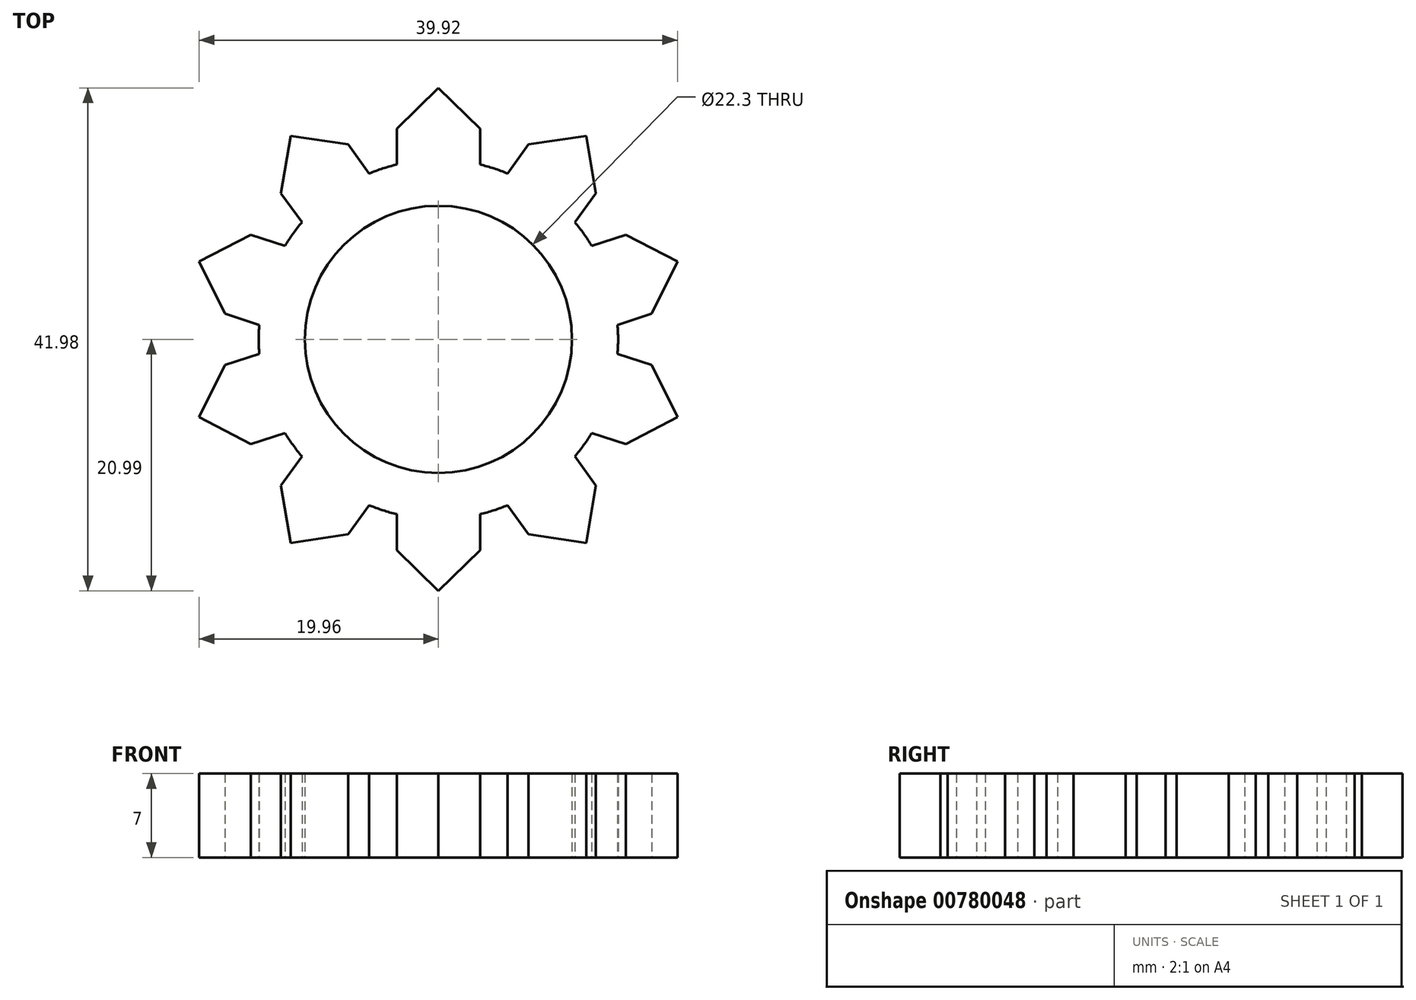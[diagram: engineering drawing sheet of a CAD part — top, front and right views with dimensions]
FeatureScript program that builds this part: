
annotation { "Feature Type Name" : "Feature", "Feature Type Description" : "" }
export const myFeature = defineFeature(function(context is Context, id is Id, definition is map)
    precondition{}
    {
        {
            var Q0;
            Q0=qCreatedBy(makeId("Top.planeOp"),FACE);
            var sketch = newSketch(context, id + "F0", { "sketchPlane" : qUnion([Q0])});
            skCircle(sketch, "E0", {"center": v(0, 0) * mm, "radius": 11.15 * mm});
            skCircle(sketch, "E1", {"center": v(0, 0) * mm, "radius": 15 * mm});
            skLineSegment(sketch, "E2", {"start": v(3.47, 14.6) * mm, "end": v(3.47, 17.6) * mm});
            skLineSegment(sketch, "E3", {"start": v(3.47, 17.6) * mm, "end": v(0, 21) * mm});
            skLineSegment(sketch, "E4.MirrorCS", {"start": v(-3.47, 14.6) * mm, "end": v(-3.47, 17.6) * mm});
            skLineSegment(sketch, "E5.MirrorCS", {"start": v(-3.47, 17.6) * mm, "end": v(0, 21) * mm});
            skLineSegment(sketch, "E6.1.0", {"start": v(-13.15, 12.2) * mm, "end": v(-12.34, 16.98) * mm});
            skLineSegment(sketch, "E6.1.1", {"start": v(-11.39, 9.77) * mm, "end": v(-13.15, 12.2) * mm});
            skLineSegment(sketch, "E6.1.2", {"start": v(-7.53, 16.27) * mm, "end": v(-12.34, 16.98) * mm});
            skLineSegment(sketch, "E6.1.3", {"start": v(-5.77, 13.85) * mm, "end": v(-7.53, 16.27) * mm});
            skLineSegment(sketch, "E6.1.4", {"start": v(-13.15, 12.2) * mm, "end": v(-12.34, 16.98) * mm});
            skLineSegment(sketch, "E6.2.0", {"start": v(-17.8, 2.13) * mm, "end": v(-19.96, 6.49) * mm});
            skLineSegment(sketch, "E6.2.1", {"start": v(-14.95, 1.2) * mm, "end": v(-17.8, 2.13) * mm});
            skLineSegment(sketch, "E6.2.2", {"start": v(-15.66, 8.74) * mm, "end": v(-19.96, 6.49) * mm});
            skLineSegment(sketch, "E6.2.3", {"start": v(-12.8, 7.81) * mm, "end": v(-15.66, 8.74) * mm});
            skLineSegment(sketch, "E6.2.4", {"start": v(-17.8, 2.13) * mm, "end": v(-19.96, 6.49) * mm});
            skLineSegment(sketch, "E6.3.0", {"start": v(-15.66, -8.74) * mm, "end": v(-19.96, -6.49) * mm});
            skLineSegment(sketch, "E6.3.1", {"start": v(-12.8, -7.81) * mm, "end": v(-15.66, -8.74) * mm});
            skLineSegment(sketch, "E6.3.2", {"start": v(-17.8, -2.13) * mm, "end": v(-19.96, -6.49) * mm});
            skLineSegment(sketch, "E6.3.3", {"start": v(-14.95, -1.2) * mm, "end": v(-17.8, -2.13) * mm});
            skLineSegment(sketch, "E6.3.4", {"start": v(-15.66, -8.74) * mm, "end": v(-19.96, -6.49) * mm});
            skLineSegment(sketch, "E6.4.0", {"start": v(-7.53, -16.27) * mm, "end": v(-12.34, -16.98) * mm});
            skLineSegment(sketch, "E6.4.1", {"start": v(-5.77, -13.85) * mm, "end": v(-7.53, -16.27) * mm});
            skLineSegment(sketch, "E6.4.2", {"start": v(-13.15, -12.2) * mm, "end": v(-12.34, -16.98) * mm});
            skLineSegment(sketch, "E6.4.3", {"start": v(-11.39, -9.77) * mm, "end": v(-13.15, -12.2) * mm});
            skLineSegment(sketch, "E6.4.4", {"start": v(-7.53, -16.27) * mm, "end": v(-12.34, -16.98) * mm});
            skLineSegment(sketch, "E6.5.0", {"start": v(3.47, -17.6) * mm, "end": v(0, -21) * mm});
            skLineSegment(sketch, "E6.5.1", {"start": v(3.47, -14.6) * mm, "end": v(3.47, -17.6) * mm});
            skLineSegment(sketch, "E6.5.2", {"start": v(-3.47, -17.6) * mm, "end": v(0, -21) * mm});
            skLineSegment(sketch, "E6.5.3", {"start": v(-3.47, -14.6) * mm, "end": v(-3.47, -17.6) * mm});
            skLineSegment(sketch, "E6.5.4", {"start": v(3.47, -17.6) * mm, "end": v(0, -21) * mm});
            skLineSegment(sketch, "E6.6.0", {"start": v(13.15, -12.2) * mm, "end": v(12.34, -16.98) * mm});
            skLineSegment(sketch, "E6.6.1", {"start": v(11.39, -9.77) * mm, "end": v(13.15, -12.2) * mm});
            skLineSegment(sketch, "E6.6.2", {"start": v(7.53, -16.27) * mm, "end": v(12.34, -16.98) * mm});
            skLineSegment(sketch, "E6.6.3", {"start": v(5.77, -13.85) * mm, "end": v(7.53, -16.27) * mm});
            skLineSegment(sketch, "E6.6.4", {"start": v(13.15, -12.2) * mm, "end": v(12.34, -16.98) * mm});
            skLineSegment(sketch, "E6.7.0", {"start": v(17.8, -2.13) * mm, "end": v(19.96, -6.49) * mm});
            skLineSegment(sketch, "E6.7.1", {"start": v(14.95, -1.2) * mm, "end": v(17.8, -2.13) * mm});
            skLineSegment(sketch, "E6.7.2", {"start": v(15.66, -8.74) * mm, "end": v(19.96, -6.49) * mm});
            skLineSegment(sketch, "E6.7.3", {"start": v(12.8, -7.81) * mm, "end": v(15.66, -8.74) * mm});
            skLineSegment(sketch, "E6.7.4", {"start": v(17.8, -2.13) * mm, "end": v(19.96, -6.49) * mm});
            skLineSegment(sketch, "E6.8.0", {"start": v(15.66, 8.74) * mm, "end": v(19.96, 6.49) * mm});
            skLineSegment(sketch, "E6.8.1", {"start": v(12.8, 7.81) * mm, "end": v(15.66, 8.74) * mm});
            skLineSegment(sketch, "E6.8.2", {"start": v(17.8, 2.13) * mm, "end": v(19.96, 6.49) * mm});
            skLineSegment(sketch, "E6.8.3", {"start": v(14.95, 1.2) * mm, "end": v(17.8, 2.13) * mm});
            skLineSegment(sketch, "E6.8.4", {"start": v(15.66, 8.74) * mm, "end": v(19.96, 6.49) * mm});
            skLineSegment(sketch, "E6.9.0", {"start": v(7.53, 16.27) * mm, "end": v(12.34, 16.98) * mm});
            skLineSegment(sketch, "E6.9.1", {"start": v(5.77, 13.85) * mm, "end": v(7.53, 16.27) * mm});
            skLineSegment(sketch, "E6.9.2", {"start": v(13.15, 12.2) * mm, "end": v(12.34, 16.98) * mm});
            skLineSegment(sketch, "E6.9.3", {"start": v(11.39, 9.77) * mm, "end": v(13.15, 12.2) * mm});
            skLineSegment(sketch, "E6.9.4", {"start": v(7.53, 16.27) * mm, "end": v(12.34, 16.98) * mm});
            skSolve(sketch);
        }
        {
            var Q0;
            Q0 = qSketchRegion(id + "F0", true);
            extrude(context, id + "F1", {"entities" : qUnion([Q0]), "depth" : 7 * mm, "offsetDistance" : 25 * mm});
        }
    });
